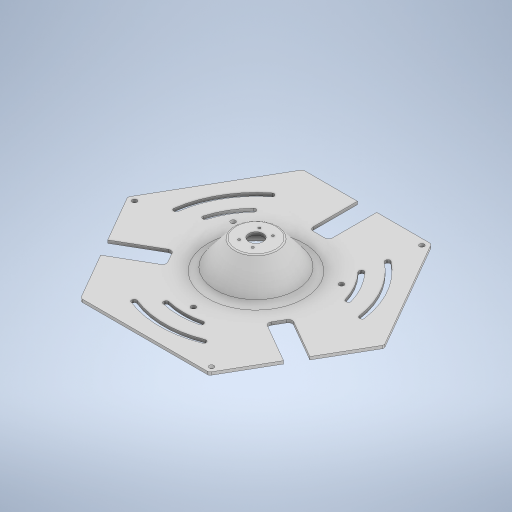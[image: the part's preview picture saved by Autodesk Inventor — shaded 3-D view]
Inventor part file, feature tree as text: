
AUTODESK INVENTOR PART (.ipt)
format: ipt  version: 2023 (Build 270158000, 158)  size: 993,280 bytes
history: native  units: mm
features: extrude x11, sketch x11, fillet x7, chamfer x2, other x1
ambient origin geometry x8: Origin, YZ Plane, XZ Plane, XY Plane, X Axis, Y Axis, Z Axis, Center Point
bodies: Body1 (feature_tree)
feature tree (32):
  other  "Bryła1"
  extrude  "Wyciągnięcie proste1"  Depth=231.0mm
  extrude  "Wyciągnięcie proste2"  Depth=3.0mm TaperAngle=0.0deg
  extrude  "Wyciągnięcie proste3"  Depth=5.0mm
  extrude  "Wyciągnięcie proste4"  TaperAngle=0.0deg  [1 undecoded]
  extrude  "Wyciągnięcie proste5"  Depth=5.0mm
  extrude  "Wyciągnięcie proste6"  Depth=3.0mm TaperAngle=0.0deg
  sketch  "Szkic7"
  fillet  "Zaokrąglenie1"  Radius=218.5mm
  fillet  "Zaokrąglenie2"  Radius=5.0mm
  fillet  "Zaokrąglenie3"  Radius=218.5mm
  extrude  "Wyciągnięcie proste7"  Depth=218.5mm
  sketch  "Szkic10"
  chamfer  "Faza1"  Distance=56.684mm
  extrude  "Wyciągnięcie proste8"  Depth=50.0mm
  chamfer  "Faza2"  Distance=20.0mm
  fillet  "Zaokrąglenie4"  Radius=3.0mm
  extrude  "Wyciągnięcie proste9"  Depth=56.684mm
  extrude  "Wyciągnięcie proste10"  Depth=50.0mm
  fillet  "Zaokrąglenie5"  Radius=20.0mm
  extrude  "Wyciągnięcie proste11"  Depth=3.0mm TaperAngle=0.0deg
  fillet  "Zaokrąglenie6"  Radius=56.684mm
  fillet  "Zaokrąglenie7"  Radius=50.0mm
  sketch  "Szkic1"
  sketch  "Szkic2"
  sketch  "Szkic3"
  sketch  "Szkic4"
  sketch  "Szkic5"
  sketch  "Szkic6"
  sketch  "Szkic9"
  sketch  "Szkic11"
  sketch  "Szkic12"
note: 1 required parameter value undecoded (feature->parameter linkage not recoverable at this tier; creation-order binding heuristic only, values carry confidence <= 0.55)
